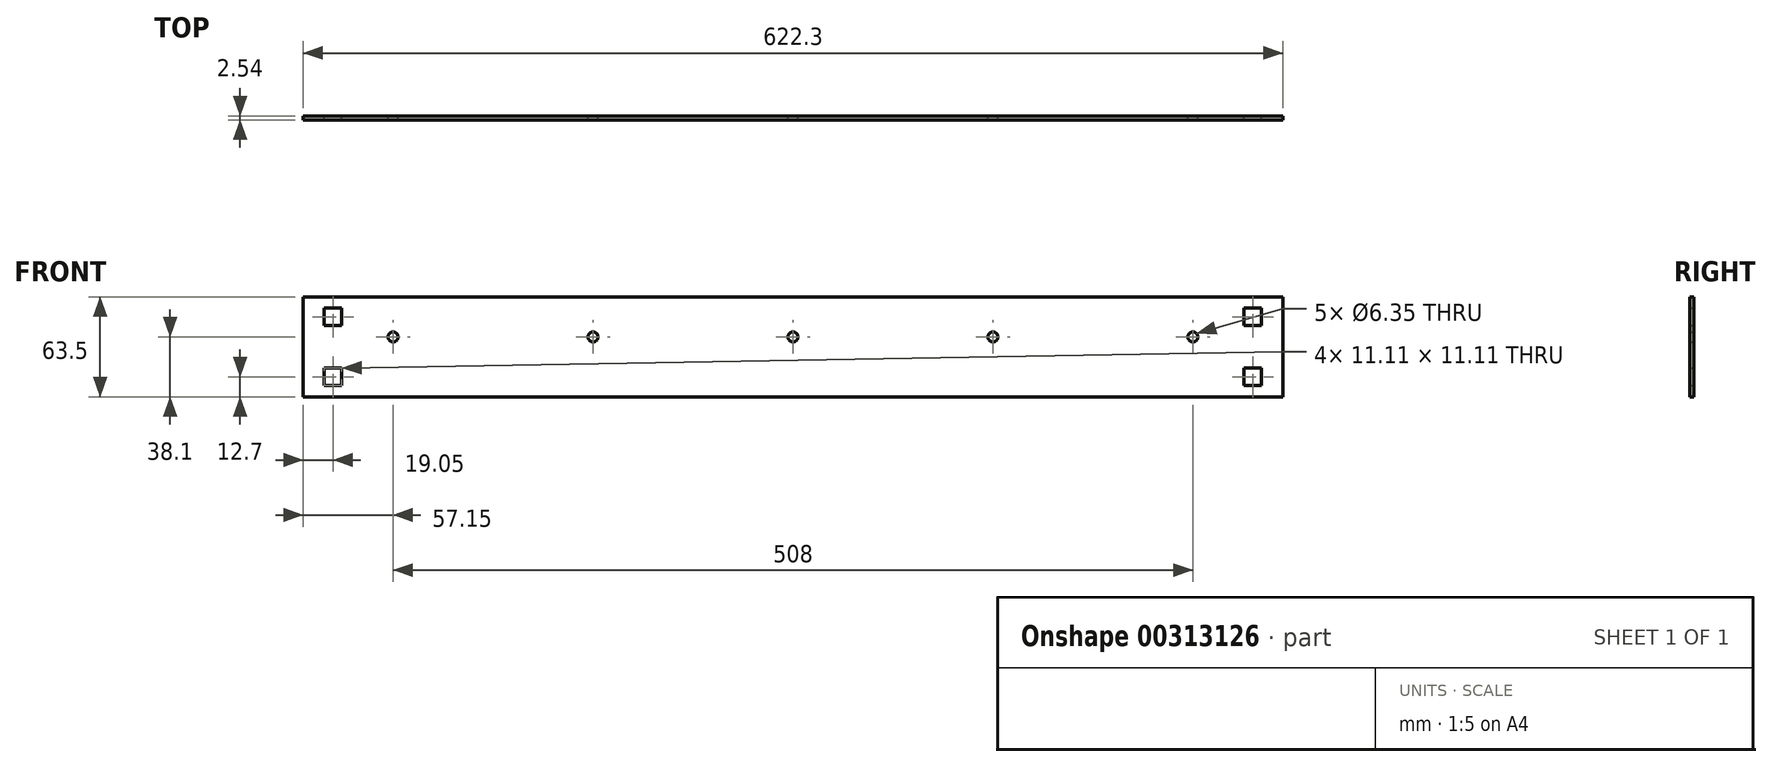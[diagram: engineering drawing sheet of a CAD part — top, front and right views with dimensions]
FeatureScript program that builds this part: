
annotation { "Feature Type Name" : "Feature", "Feature Type Description" : "" }
export const myFeature = defineFeature(function(context is Context, id is Id, definition is map)
    precondition{}
    {
        {
            var Q0;
            Q0=qCreatedBy(makeId("Front.planeOp"),FACE);
            var sketch = newSketch(context, id + "F0", { "sketchPlane" : qUnion([Q0])});
            skLineSegment(sketch, "E0.bottom", {"start": v(311.15, 31.75) * mm, "end": v(-311.15, 31.75) * mm});
            skLineSegment(sketch, "E0.top", {"start": v(311.15, -31.75) * mm, "end": v(-311.15, -31.75) * mm});
            skLineSegment(sketch, "E0.left", {"start": v(311.15, 31.75) * mm, "end": v(311.15, -31.75) * mm});
            skLineSegment(sketch, "E0.right", {"start": v(-311.15, 31.75) * mm, "end": v(-311.15, -31.75) * mm});
            skPoint(sketch, "E0.middle", {"position": v(0, 0) * mm});
            skLineSegment(sketch, "E1.bottom", {"start": v(-286.54, 13.5) * mm, "end": v(-297.66, 13.5) * mm});
            skLineSegment(sketch, "E1.top", {"start": v(-286.54, 24.6) * mm, "end": v(-297.66, 24.6) * mm});
            skLineSegment(sketch, "E1.left", {"start": v(-286.54, 13.5) * mm, "end": v(-286.54, 24.6) * mm});
            skLineSegment(sketch, "E1.right", {"start": v(-297.66, 13.5) * mm, "end": v(-297.66, 24.6) * mm});
            skPoint(sketch, "E1.middle", {"position": v(-292.1, 19.05) * mm});
            skLineSegment(sketch, "E2.bottom", {"start": v(-297.66, -24.6) * mm, "end": v(-286.54, -24.6) * mm});
            skLineSegment(sketch, "E2.top", {"start": v(-297.66, -13.5) * mm, "end": v(-286.54, -13.5) * mm});
            skLineSegment(sketch, "E2.left", {"start": v(-297.66, -24.6) * mm, "end": v(-297.66, -13.5) * mm});
            skLineSegment(sketch, "E2.right", {"start": v(-286.54, -24.6) * mm, "end": v(-286.54, -13.5) * mm});
            skPoint(sketch, "E2.middle", {"position": v(-292.1, -19.05) * mm});
            skPoint(sketch, "E3.1.0.0", {"position": v(292.1, -19.05) * mm});
            skPoint(sketch, "E3.1.0.1", {"position": v(292.1, 19.05) * mm});
            skLineSegment(sketch, "E3.1.0.2", {"start": v(286.54, 13.5) * mm, "end": v(286.54, 24.6) * mm});
            skLineSegment(sketch, "E3.1.0.3", {"start": v(297.66, 13.5) * mm, "end": v(297.66, 24.6) * mm});
            skLineSegment(sketch, "E3.1.0.4", {"start": v(297.66, 24.6) * mm, "end": v(286.54, 24.6) * mm});
            skLineSegment(sketch, "E3.1.0.5", {"start": v(297.66, 13.5) * mm, "end": v(286.54, 13.5) * mm});
            skLineSegment(sketch, "E3.1.0.6", {"start": v(286.54, -24.6) * mm, "end": v(297.66, -24.6) * mm});
            skLineSegment(sketch, "E3.1.0.7", {"start": v(286.54, -13.5) * mm, "end": v(297.66, -13.5) * mm});
            skLineSegment(sketch, "E3.1.0.8", {"start": v(286.54, -24.6) * mm, "end": v(286.54, -13.5) * mm});
            skLineSegment(sketch, "E3.1.0.9", {"start": v(297.66, -24.6) * mm, "end": v(297.66, -13.5) * mm});
            skLineSegment(sketch, "E3.direction1", {"start": v(-297.66, -24.6) * mm, "end": v(286.54, -24.6) * mm, "construction": true});
            skCircle(sketch, "E4", {"center": v(-254, 6.35) * mm, "radius": 3.18 * mm});
            skCircle(sketch, "E5.1.0.0", {"center": v(-127, 6.35) * mm, "radius": 3.18 * mm});
            skCircle(sketch, "E5.2.0.0", {"center": v(0, 6.35) * mm, "radius": 3.18 * mm});
            skCircle(sketch, "E5.3.0.0", {"center": v(127, 6.35) * mm, "radius": 3.18 * mm});
            skCircle(sketch, "E5.4.0.0", {"center": v(254, 6.35) * mm, "radius": 3.18 * mm});
            skLineSegment(sketch, "E5.direction1", {"start": v(-254, 6.35) * mm, "end": v(-127, 6.35) * mm, "construction": true});
            skSolve(sketch);
        }
        {
            var Q0;
            Q0=makeQuery(id+"F0.imprint","IMPRINT",FACE,{"disambiguationData":[TD([[makeQuery(id+"F0.imprint","IMPRINT",EDGE,{"derivedFrom":sQuery(id+"F0.wireOp",EDGE,"E0.bottom")}),1.0]])]});
            extrude(context, id + "F1", {"entities" : qUnion([Q0]), "endBound" : BoundingType.SYMMETRIC, "depth" : 2.54 * mm});
        }
    });
